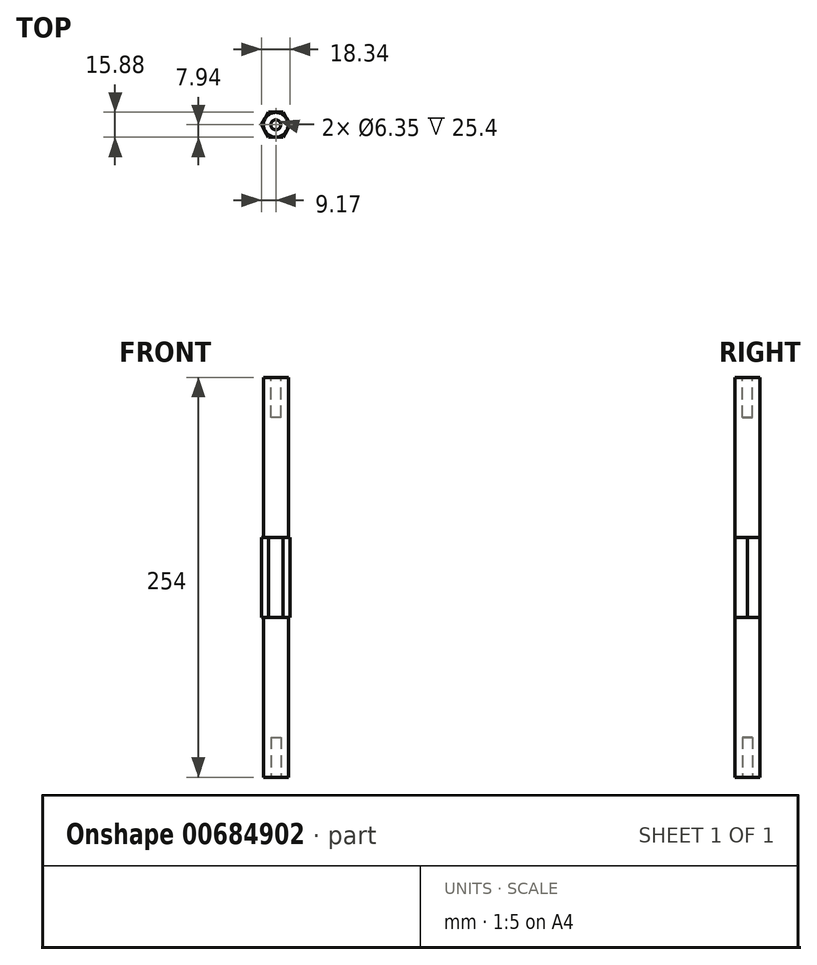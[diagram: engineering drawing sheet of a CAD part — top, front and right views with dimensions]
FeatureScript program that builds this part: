
annotation { "Feature Type Name" : "Feature", "Feature Type Description" : "" }
export const myFeature = defineFeature(function(context is Context, id is Id, definition is map)
    precondition{}
    {
        {
            var Q0;
            Q0=qCreatedBy(makeId("Top.planeOp"),FACE);
            var sketch = newSketch(context, id + "F0", { "sketchPlane" : qUnion([Q0])});
            skCircle(sketch, "E0", {"center": v(0, 0) * mm, "radius": 7.94 * mm, "construction": true});
            skLineSegment(sketch, "E1", {"start": v(-56.7, 0) * mm, "end": v(63.32, 0) * mm, "construction": true});
            skLineSegment(sketch, "E2", {"start": v(0, -40.46) * mm, "end": v(0, 43.76) * mm, "construction": true});
            skLineSegment(sketch, "E3", {"start": v(0, 0) * mm, "end": v(-27.5, -15.88) * mm, "construction": true});
            skLineSegment(sketch, "E4", {"start": v(0, 0) * mm, "end": v(28.61, -16.52) * mm, "construction": true});
            skLineSegment(sketch, "E5.MirrorCS", {"start": v(0, 0) * mm, "end": v(28.61, 16.52) * mm, "construction": true});
            skLineSegment(sketch, "E6.MirrorCS", {"start": v(0, 0) * mm, "end": v(-27.5, 15.88) * mm, "construction": true});
            skLineSegment(sketch, "E7", {"start": v(-9.17, 0) * mm, "end": v(-4.58, -7.94) * mm});
            skLineSegment(sketch, "E8", {"start": v(-9.17, 0) * mm, "end": v(-4.58, 7.94) * mm});
            skLineSegment(sketch, "E9.trimOffspring", {"start": v(-4.58, -7.94) * mm, "end": v(26.02, -7.94) * mm});
            skLineSegment(sketch, "E10.trimOffspring", {"start": v(-4.58, 7.94) * mm, "end": v(4.58, 7.94) * mm});
            skLineSegment(sketch, "E11.MirrorCS", {"start": v(9.17, 0) * mm, "end": v(4.58, -7.94) * mm});
            skLineSegment(sketch, "E12.MirrorCS", {"start": v(9.17, 0) * mm, "end": v(4.58, 7.94) * mm});
            skSolve(sketch);
        }
        {
            var Q0;
            Q0 = qSketchRegion(id + "F0", true);
            extrude(context, id + "F1", {"entities" : qUnion([Q0]), "depth" : 254 * mm, "offsetDistance" : 25.4 * mm});
        }
        {
            var Q0;
            Q0=makeQuery(id+"F1.opExtrude","CAP_FACE",FACE,{"disambiguationData":[OSD([sQuery(id+"F0.wireOp",EDGE,"E7"),sQuery(id+"F0.wireOp",EDGE,"E8"),sQuery(id+"F0.wireOp",EDGE,"E9.trimOffspring"),sQuery(id+"F0.wireOp",EDGE,"E10.trimOffspring"),sQuery(id+"F0.wireOp",EDGE,"E11.MirrorCS"),sQuery(id+"F0.wireOp",EDGE,"E12.MirrorCS")])],"isStart":true});
            var sketch = newSketch(context, id + "F2", { "sketchPlane" : qUnion([Q0])});
            skCircle(sketch, "E13", {"center": v(0, 0) * mm, "radius": 7.94 * mm});
            skCircle(sketch, "E14", {"center": v(0, 0) * mm, "radius": 9.17 * mm});
            skSolve(sketch);
        }
        {
            var Q0;
            Q0 = qSketchRegion(id + "F2", true);
            extrude(context, id + "F3", {"entities" : qUnion([Q0]), "operationType" : NewBodyOperationType.REMOVE, "oppositeDirection" : true, "depth" : 101.6 * mm, "offsetDistance" : 25.4 * mm});
        }
        {
            var Q0;
            Q0=makeQuery(id+"F1.opExtrude","CAP_FACE",FACE,{"disambiguationData":[OSD([sQuery(id+"F0.wireOp",EDGE,"E7"),sQuery(id+"F0.wireOp",EDGE,"E8"),sQuery(id+"F0.wireOp",EDGE,"E9.trimOffspring"),sQuery(id+"F0.wireOp",EDGE,"E10.trimOffspring"),sQuery(id+"F0.wireOp",EDGE,"E11.MirrorCS"),sQuery(id+"F0.wireOp",EDGE,"E12.MirrorCS")])],"isStart":false});
            var sketch = newSketch(context, id + "F4", { "sketchPlane" : qUnion([Q0])});
            skCircle(sketch, "E15", {"center": v(0, 0) * mm, "radius": 7.94 * mm});
            skCircle(sketch, "E16", {"center": v(0, 0) * mm, "radius": 9.17 * mm});
            skSolve(sketch);
        }
        {
            var Q0;
            Q0 = qSketchRegion(id + "F4", true);
            extrude(context, id + "F5", {"entities" : qUnion([Q0]), "operationType" : NewBodyOperationType.REMOVE, "oppositeDirection" : true, "depth" : 101.6 * mm, "offsetDistance" : 25.4 * mm});
        }
        {
            var Q0;
            Q0=makeQuery(id+"F1.opExtrude","CAP_FACE",FACE,{"disambiguationData":[OSD([sQuery(id+"F0.wireOp",EDGE,"E7"),sQuery(id+"F0.wireOp",EDGE,"E8"),sQuery(id+"F0.wireOp",EDGE,"E9.trimOffspring"),sQuery(id+"F0.wireOp",EDGE,"E10.trimOffspring"),sQuery(id+"F0.wireOp",EDGE,"E11.MirrorCS"),sQuery(id+"F0.wireOp",EDGE,"E12.MirrorCS")])],"isStart":true});
            var sketch = newSketch(context, id + "F6", { "sketchPlane" : qUnion([Q0])});
            skCircle(sketch, "E17", {"center": v(0, 0) * mm, "radius": 3.18 * mm});
            skSolve(sketch);
        }
        {
            var Q0;
            Q0 = qSketchRegion(id + "F6", true);
            extrude(context, id + "F7", {"entities" : qUnion([Q0]), "operationType" : NewBodyOperationType.REMOVE, "oppositeDirection" : true, "depth" : 25.4 * mm, "offsetDistance" : 25.4 * mm});
        }
        {
            var Q0;
            Q0=makeQuery(id+"F1.opExtrude","CAP_FACE",FACE,{"disambiguationData":[OSD([sQuery(id+"F0.wireOp",EDGE,"E7"),sQuery(id+"F0.wireOp",EDGE,"E8"),sQuery(id+"F0.wireOp",EDGE,"E9.trimOffspring"),sQuery(id+"F0.wireOp",EDGE,"E10.trimOffspring"),sQuery(id+"F0.wireOp",EDGE,"E11.MirrorCS"),sQuery(id+"F0.wireOp",EDGE,"E12.MirrorCS")])],"isStart":false});
            var sketch = newSketch(context, id + "F8", { "sketchPlane" : qUnion([Q0])});
            skCircle(sketch, "E18", {"center": v(0, 0) * mm, "radius": 3.18 * mm});
            skSolve(sketch);
        }
        {
            var Q0;
            Q0 = qSketchRegion(id + "F8", true);
            extrude(context, id + "F9", {"entities" : qUnion([Q0]), "operationType" : NewBodyOperationType.REMOVE, "oppositeDirection" : true, "depth" : 25.4 * mm, "offsetDistance" : 25.4 * mm});
        }
    });
